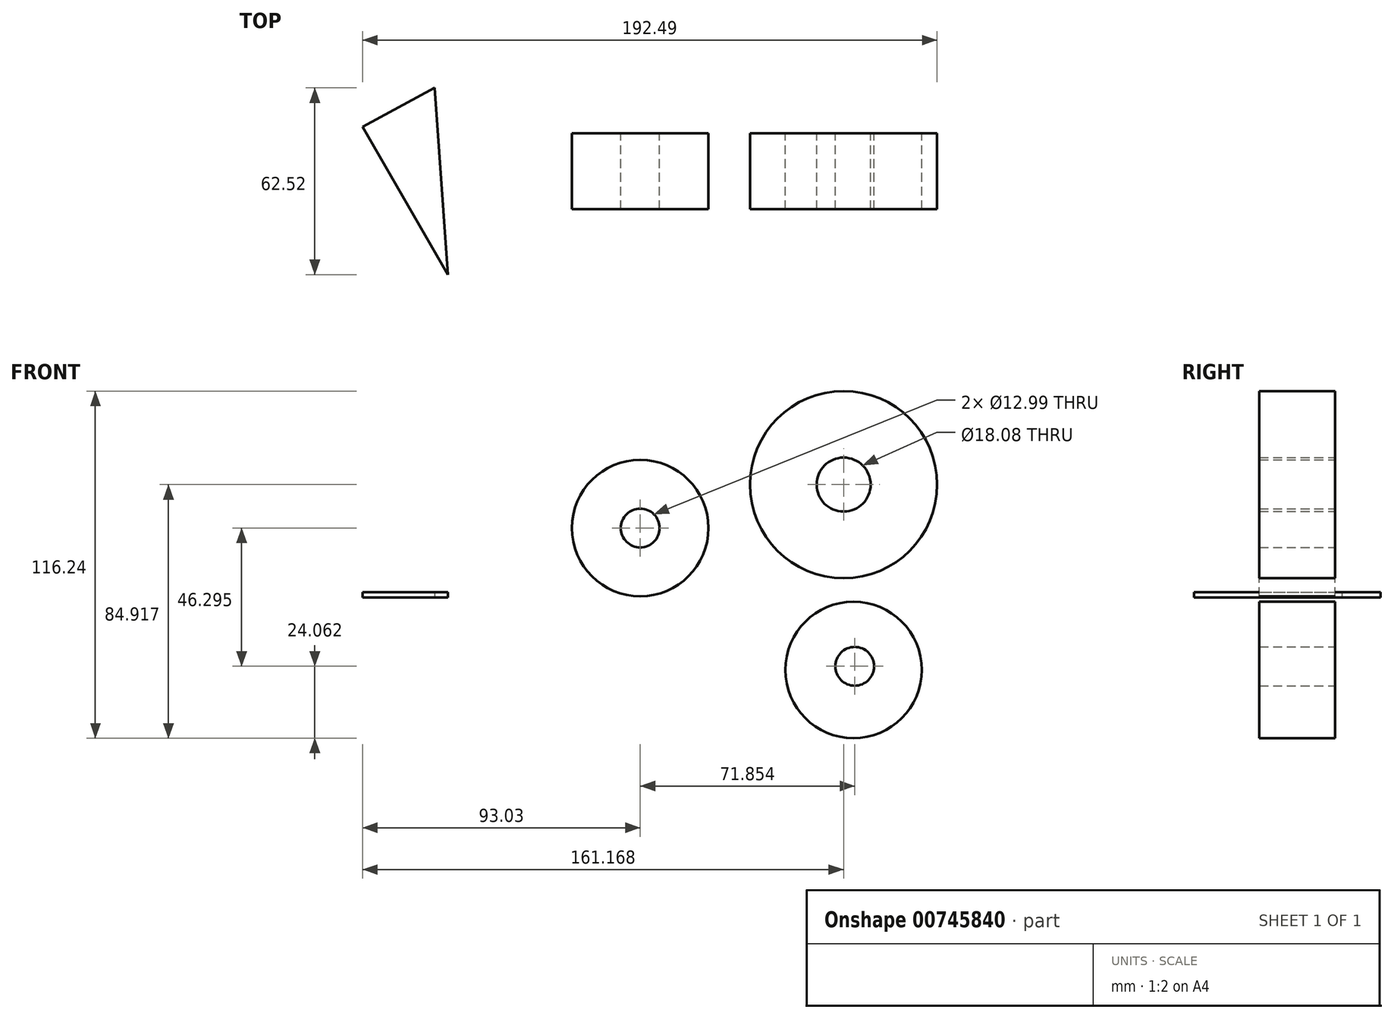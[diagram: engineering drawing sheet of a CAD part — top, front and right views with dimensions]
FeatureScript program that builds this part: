
annotation { "Feature Type Name" : "Feature", "Feature Type Description" : "" }
export const myFeature = defineFeature(function(context is Context, id is Id, definition is map)
    precondition{}
    {
        {
            var Q0;
            Q0=qCreatedBy(makeId("Top.planeOp"),FACE);
            var sketch = newSketch(context, id + "F0", { "sketchPlane" : qUnion([Q0])});
            skLineSegment(sketch, "E0", {"start": v(-97.41, -47.27) * mm, "end": v(-101.89, 15.25) * mm});
            skLineSegment(sketch, "E1", {"start": v(-97.41, -47.27) * mm, "end": v(-126, 2.25) * mm});
            skLineSegment(sketch, "E2", {"start": v(-101.89, 15.25) * mm, "end": v(-126, 2.25) * mm});
            skSolve(sketch);
        }
        {
            var Q0;
            Q0=makeQuery(id+"F0.imprint","IMPRINT",FACE,{"disambiguationData":[TD([[makeQuery(id+"F0.imprint","IMPRINT",EDGE,{"derivedFrom":sQuery(id+"F0.wireOp",EDGE,"E0")}),1.0]])]});
            extrude(context, id + "F1", {"entities" : qUnion([Q0]), "depth" : 1.78 * mm, "offsetDistance" : 25.4 * mm});
        }
        {
            var Q0;
            Q0=qCreatedBy(makeId("Front.planeOp"),FACE);
            var sketch = newSketch(context, id + "F2", { "sketchPlane" : qUnion([Q0])});
            skCircle(sketch, "E3", {"center": v(-32.98, 23.3) * mm, "radius": 22.85 * mm});
            skCircle(sketch, "E4", {"center": v(-32.98, 23.3) * mm, "radius": 6.5 * mm});
            skCircle(sketch, "E5", {"center": v(35.16, 37.86) * mm, "radius": 31.32 * mm});
            skCircle(sketch, "E6", {"center": v(35.16, 37.86) * mm, "radius": 9.04 * mm});
            skCircle(sketch, "E7", {"center": v(38.47, -24.2) * mm, "radius": 22.85 * mm});
            skCircle(sketch, "E8", {"center": v(38.87, -23) * mm, "radius": 6.5 * mm});
            skSolve(sketch);
        }
        {
            var Q0;
            Q0 = qSketchRegion(id + "F2", true);
            extrude(context, id + "F3", {"entities" : qUnion([Q0]), "depth" : 25.4 * mm, "offsetDistance" : 25.4 * mm});
        }
    });
